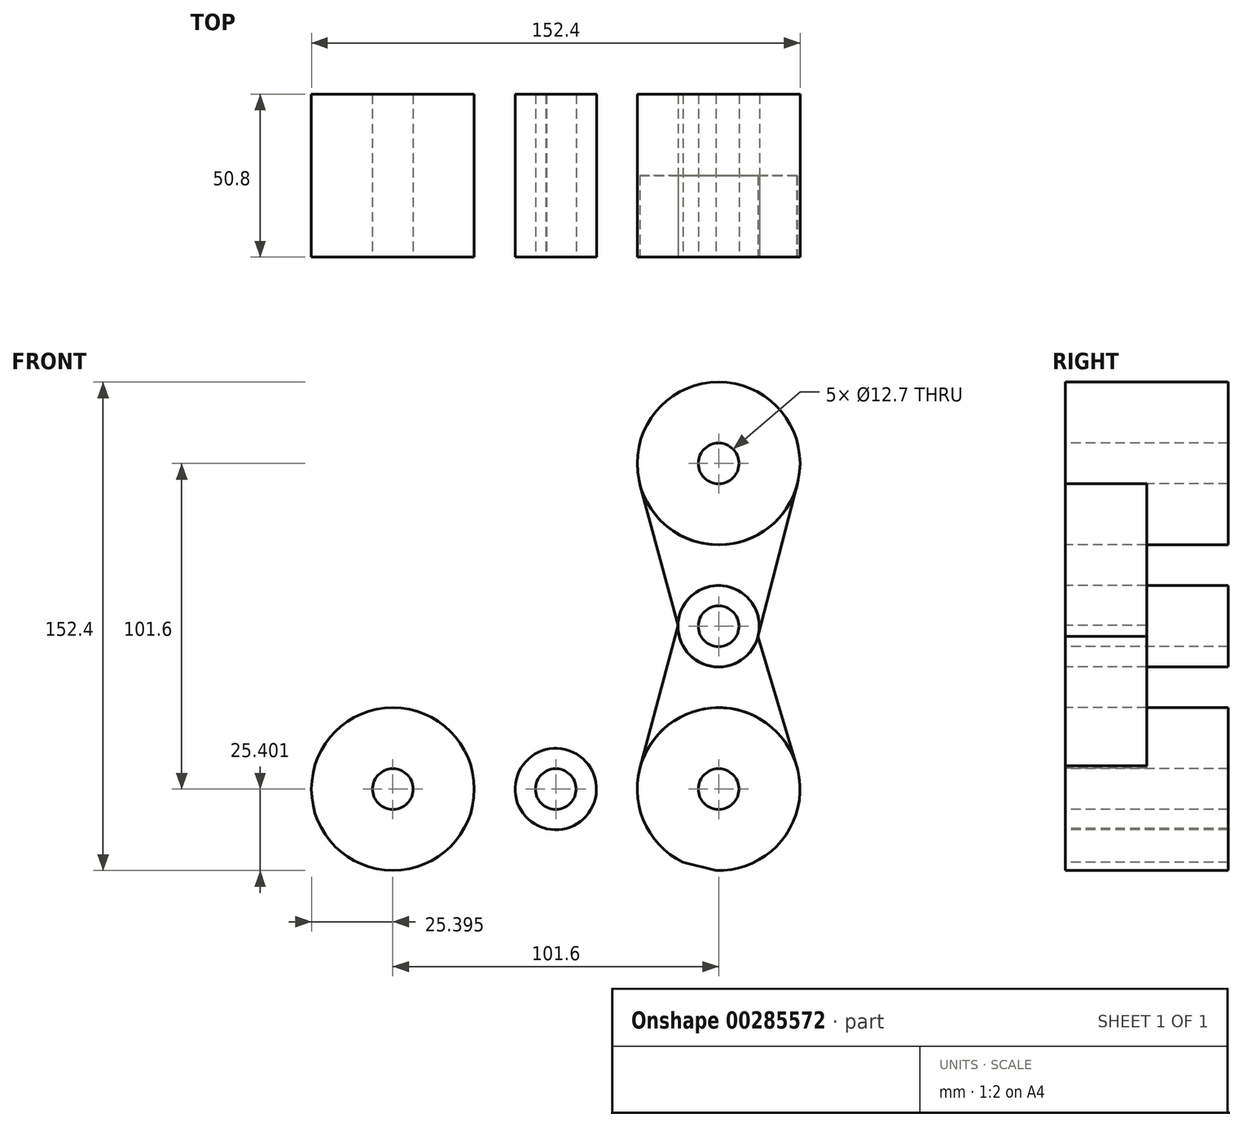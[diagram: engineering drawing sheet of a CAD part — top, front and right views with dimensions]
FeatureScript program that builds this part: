
annotation { "Feature Type Name" : "Feature", "Feature Type Description" : "" }
export const myFeature = defineFeature(function(context is Context, id is Id, definition is map)
    precondition{}
    {
        {
            var Q0;
            Q0=qCreatedBy(makeId("Front.planeOp"),FACE);
            var sketch = newSketch(context, id + "F0", { "sketchPlane" : qUnion([Q0])});
            skLineSegment(sketch, "E0", {"start": v(87.94, -74.96) * mm, "end": v(138.74, -74.96) * mm});
            skLineSegment(sketch, "E1", {"start": v(138.74, -74.96) * mm, "end": v(138.74, -24.16) * mm});
            skLineSegment(sketch, "E2", {"start": v(87.94, -74.96) * mm, "end": v(37.14, -74.96) * mm});
            skLineSegment(sketch, "E3", {"start": v(138.74, -24.16) * mm, "end": v(138.74, 26.64) * mm});
            skCircle(sketch, "E4", {"center": v(138.74, 26.64) * mm, "radius": 25.4 * mm});
            skCircle(sketch, "E5", {"center": v(138.74, -74.96) * mm, "radius": 25.4 * mm});
            skCircle(sketch, "E6", {"center": v(37.14, -74.96) * mm, "radius": 25.4 * mm});
            skCircle(sketch, "E7", {"center": v(138.74, -24.16) * mm, "radius": 12.7 * mm});
            skCircle(sketch, "E8", {"center": v(87.94, -74.96) * mm, "radius": 12.7 * mm});
            skLineSegment(sketch, "E9", {"start": v(163.33, 20.3) * mm, "end": v(151.03, -27.33) * mm});
            skLineSegment(sketch, "E10", {"start": v(151.03, -27.33) * mm, "end": v(163.08, -67.7) * mm});
            skLineSegment(sketch, "E11", {"start": v(84.76, -87.26) * mm, "end": v(44.4, -99.3) * mm});
            skLineSegment(sketch, "E12", {"start": v(114.2, 20.04) * mm, "end": v(126.04, -23.9) * mm});
            skLineSegment(sketch, "E13", {"start": v(126.04, -23.9) * mm, "end": v(114.19, -68.43) * mm});
            skLineSegment(sketch, "E14", {"start": v(114.19, -68.43) * mm, "end": v(91.01, -62.64) * mm});
            skLineSegment(sketch, "E15", {"start": v(91.01, -62.64) * mm, "end": v(43.49, -50.37) * mm});
            skLineSegment(sketch, "E16", {"start": v(84.76, -87.26) * mm, "end": v(137.94, -100.35) * mm});
            skSolve(sketch);
        }
        {
            var Q0;
            {var subQ0=sQuery(id+"F0.wireOp",EDGE,"E4");var subQ1=makeQuery(id+"F0.imprint","INTERSECT",VERTEX,{"derivedFrom":[subQ0,sQuery(id+"F0.wireOp",EDGE,"E12")]});Q0=makeQuery(id+"F0.imprint","IMPRINT",FACE,{"disambiguationData":[TD([[makeQuery(id+"F0.imprint","IMPRINT",EDGE,{"disambiguationData":[TD([[subQ1,-1.0]])],"derivedFrom":subQ0}),1.0]])]});}
            var Q1;
            {var subQ0=sQuery(id+"F0.wireOp",EDGE,"E3");var subQ1=sQuery(id+"F0.wireOp",EDGE,"E1");var subQ2=makeQuery(id+"F0.imprint","INTERSECT",VERTEX,{"derivedFrom":[subQ1,subQ0]});Q1=makeQuery(id+"F0.imprint","IMPRINT",FACE,{"disambiguationData":[TD([[makeQuery(id+"F0.imprint","IMPRINT",EDGE,{"disambiguationData":[TD([[subQ2,1.0]])],"derivedFrom":subQ1}),1.0]])]});}
            var Q2;
            {var subQ0=sQuery(id+"F0.wireOp",EDGE,"E3");var subQ1=sQuery(id+"F0.wireOp",EDGE,"E1");var subQ2=makeQuery(id+"F0.imprint","INTERSECT",VERTEX,{"derivedFrom":[subQ1,subQ0]});Q2=makeQuery(id+"F0.imprint","IMPRINT",FACE,{"disambiguationData":[TD([[makeQuery(id+"F0.imprint","IMPRINT",EDGE,{"disambiguationData":[TD([[subQ2,1.0]])],"derivedFrom":subQ1}),-1.0]])]});}
            var Q3;
            {var subQ0=sQuery(id+"F0.wireOp",EDGE,"E6");var subQ1=makeQuery(id+"F0.imprint","INTERSECT",VERTEX,{"derivedFrom":[subQ0,sQuery(id+"F0.wireOp",EDGE,"E15")]});Q3=makeQuery(id+"F0.imprint","IMPRINT",FACE,{"disambiguationData":[TD([[makeQuery(id+"F0.imprint","IMPRINT",EDGE,{"disambiguationData":[TD([[subQ1,1.0]])],"derivedFrom":subQ0}),1.0]])]});}
            var Q4;
            {var subQ0=sQuery(id+"F0.wireOp",EDGE,"E2");var subQ1=sQuery(id+"F0.wireOp",EDGE,"E0");var subQ2=makeQuery(id+"F0.imprint","INTERSECT",VERTEX,{"derivedFrom":[subQ1,subQ0]});Q4=makeQuery(id+"F0.imprint","IMPRINT",FACE,{"disambiguationData":[TD([[makeQuery(id+"F0.imprint","IMPRINT",EDGE,{"disambiguationData":[TD([[subQ2,-1.0]])],"derivedFrom":subQ1}),-1.0]])]});}
            var Q5;
            {var subQ0=sQuery(id+"F0.wireOp",EDGE,"E2");var subQ1=sQuery(id+"F0.wireOp",EDGE,"E0");var subQ2=makeQuery(id+"F0.imprint","INTERSECT",VERTEX,{"derivedFrom":[subQ1,subQ0]});Q5=makeQuery(id+"F0.imprint","IMPRINT",FACE,{"disambiguationData":[TD([[makeQuery(id+"F0.imprint","IMPRINT",EDGE,{"disambiguationData":[TD([[subQ2,-1.0]])],"derivedFrom":subQ1}),1.0]])]});}
            var Q6;
            {var subQ0=sQuery(id+"F0.wireOp",EDGE,"E1");var subQ1=sQuery(id+"F0.wireOp",EDGE,"E0");var subQ2=makeQuery(id+"F0.imprint","INTERSECT",VERTEX,{"derivedFrom":[subQ1,subQ0]});Q6=makeQuery(id+"F0.imprint","IMPRINT",FACE,{"disambiguationData":[TD([[makeQuery(id+"F0.imprint","IMPRINT",EDGE,{"disambiguationData":[TD([[subQ2,1.0]])],"derivedFrom":subQ1}),-1.0]])]});}
            var Q7;
            {var subQ0=sQuery(id+"F0.wireOp",EDGE,"E1");var subQ1=sQuery(id+"F0.wireOp",EDGE,"E0");var subQ2=makeQuery(id+"F0.imprint","INTERSECT",VERTEX,{"derivedFrom":[subQ1,subQ0]});Q7=makeQuery(id+"F0.imprint","IMPRINT",FACE,{"disambiguationData":[TD([[makeQuery(id+"F0.imprint","IMPRINT",EDGE,{"disambiguationData":[TD([[subQ2,1.0]])],"derivedFrom":subQ1}),1.0]])]});}
            extrude(context, id + "F1", {"entities" : qUnion([Q0, Q1, Q2, Q3, Q4, Q5, Q6, Q7]), "oppositeDirection" : true, "depth" : 50.8 * mm});
        }
        {
            var Q0;
            {var subQ5=sQuery(id+"F0.wireOp",EDGE,"E12");Q0=makeQuery(id+"F0.imprint","IMPRINT",FACE,{"disambiguationData":[TD([[makeQuery(id+"F0.imprint","IMPRINT",EDGE,{"derivedFrom":subQ5}),1.0]])]});}
            var Q1;
            {var subQ5=sQuery(id+"F0.wireOp",EDGE,"E9");Q1=makeQuery(id+"F0.imprint","IMPRINT",FACE,{"disambiguationData":[TD([[makeQuery(id+"F0.imprint","IMPRINT",EDGE,{"derivedFrom":subQ5}),-1.0]])]});}
            var Q2;
            {var subQ5=sQuery(id+"F0.wireOp",EDGE,"E13");Q2=makeQuery(id+"F0.imprint","IMPRINT",FACE,{"disambiguationData":[TD([[makeQuery(id+"F0.imprint","IMPRINT",EDGE,{"derivedFrom":subQ5}),1.0]])]});}
            var Q3;
            {var subQ5=sQuery(id+"F0.wireOp",EDGE,"E10");Q3=makeQuery(id+"F0.imprint","IMPRINT",FACE,{"disambiguationData":[TD([[makeQuery(id+"F0.imprint","IMPRINT",EDGE,{"derivedFrom":subQ5}),-1.0]])]});}
            extrude(context, id + "F2", {"entities" : qUnion([Q0, Q1, Q2, Q3]), "oppositeDirection" : true, "depth" : 25.4 * mm});
        }
        {
            var Q0;
            Q0=sQuery(id+"F0.wireOp",VERTEX,"E7.center");
            var Q1;
            Q1=sQuery(id+"F0.wireOp",VERTEX,"E3.end");
            var Q2;
            Q2=sQuery(id+"F0.wireOp",VERTEX,"E5.center");
            var Q3;
            Q3=sQuery(id+"F0.wireOp",VERTEX,"E2.start");
            var Q4;
            Q4=sQuery(id+"F0.wireOp",VERTEX,"E2.end");
            var Q5;
            Q5=makeQuery(id+"F1.opExtrude","SWEPT_BODY",BODY,{"disambiguationData":[OSD([sQuery(id+"F0.wireOp",EDGE,"E7")])]});
            var Q6;
            Q6=makeQuery(id+"F1.opExtrude","SWEPT_BODY",BODY,{"disambiguationData":[OSD([sQuery(id+"F0.wireOp",EDGE,"E4")])]});
            var Q7;
            Q7=makeQuery(id+"F1.opExtrude","SWEPT_BODY",BODY,{"disambiguationData":[OSD([sQuery(id+"F0.wireOp",EDGE,"E5"),sQuery(id+"F0.wireOp",EDGE,"E16")])]});
            var Q8;
            Q8=makeQuery(id+"F1.opExtrude","SWEPT_BODY",BODY,{"disambiguationData":[OSD([sQuery(id+"F0.wireOp",EDGE,"E8"),sQuery(id+"F0.wireOp",EDGE,"E16")])]});
            var Q9;
            Q9=makeQuery(id+"F1.opExtrude","SWEPT_BODY",BODY,{"disambiguationData":[OSD([sQuery(id+"F0.wireOp",EDGE,"E6")])]});
            hole(context, id + "F3", {"style" : HoleStyle.SIMPLE, "endStyle" : HoleEndStyle.THROUGH, "holeDiameter" : 12.7 * mm, "tappedDepth" : 12.7 * mm, "tapClearance" : 3, "locations" : qUnion([Q0, Q1, Q2, Q3, Q4]), "scope" : qUnion([Q5, Q6, Q7, Q8, Q9])});
        }
    });
